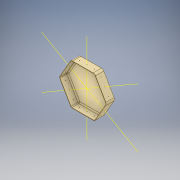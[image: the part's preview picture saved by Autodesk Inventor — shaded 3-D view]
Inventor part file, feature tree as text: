
AUTODESK INVENTOR PART (.ipt)
format: ipt  version: 2019 (Build 230136000, 136)  size: 192,512 bytes
history: native  units: mm
features: mirror x4, plane x3, other x3, extrude x2, sketch x2, fillet x2, shell x1, projected_geometry x1
ambient origin geometry x8: Origin, YZ Plane, XZ Plane, XY Plane, X Axis, Y Axis, Z Axis, Center Point
bodies: Solid1 (feature_tree)
feature tree (18):
  extrude  "Extrusion1"  Depth=30.0mm TaperAngle=0.0deg
  shell  "Shell1"  Thickness=1.5mm
  sketch  "Sketch2"  dims[d5=2.0mm d6=15.0mm d7=15.0mm d8=1.0mm d9=0.0mm d10=4.0mm d11=10.0mm d12=1.0mm]
  plane  "Work Plane1"
  plane  "Work Plane2"
  plane  "Work Plane3"
  extrude  "Extrusion2"  Depth=1.0mm
  mirror  "Mirror1"
  mirror  "Mirror2"
  mirror  "Mirror3"
  mirror  "Mirror4"
  fillet  "Fillet1"  Radius=15.0mm
  fillet  "Fillet2"  Radius=1.0mm
  other  "Work Axis1"
  other  "Work Axis2"
  other  "Work Axis3"
  sketch  "Sketch1"  dims[d0=150.0mm d2=30.0mm d3=0.0mm d4=1.5mm]
  projected_geometry  "Projected Loop1"
